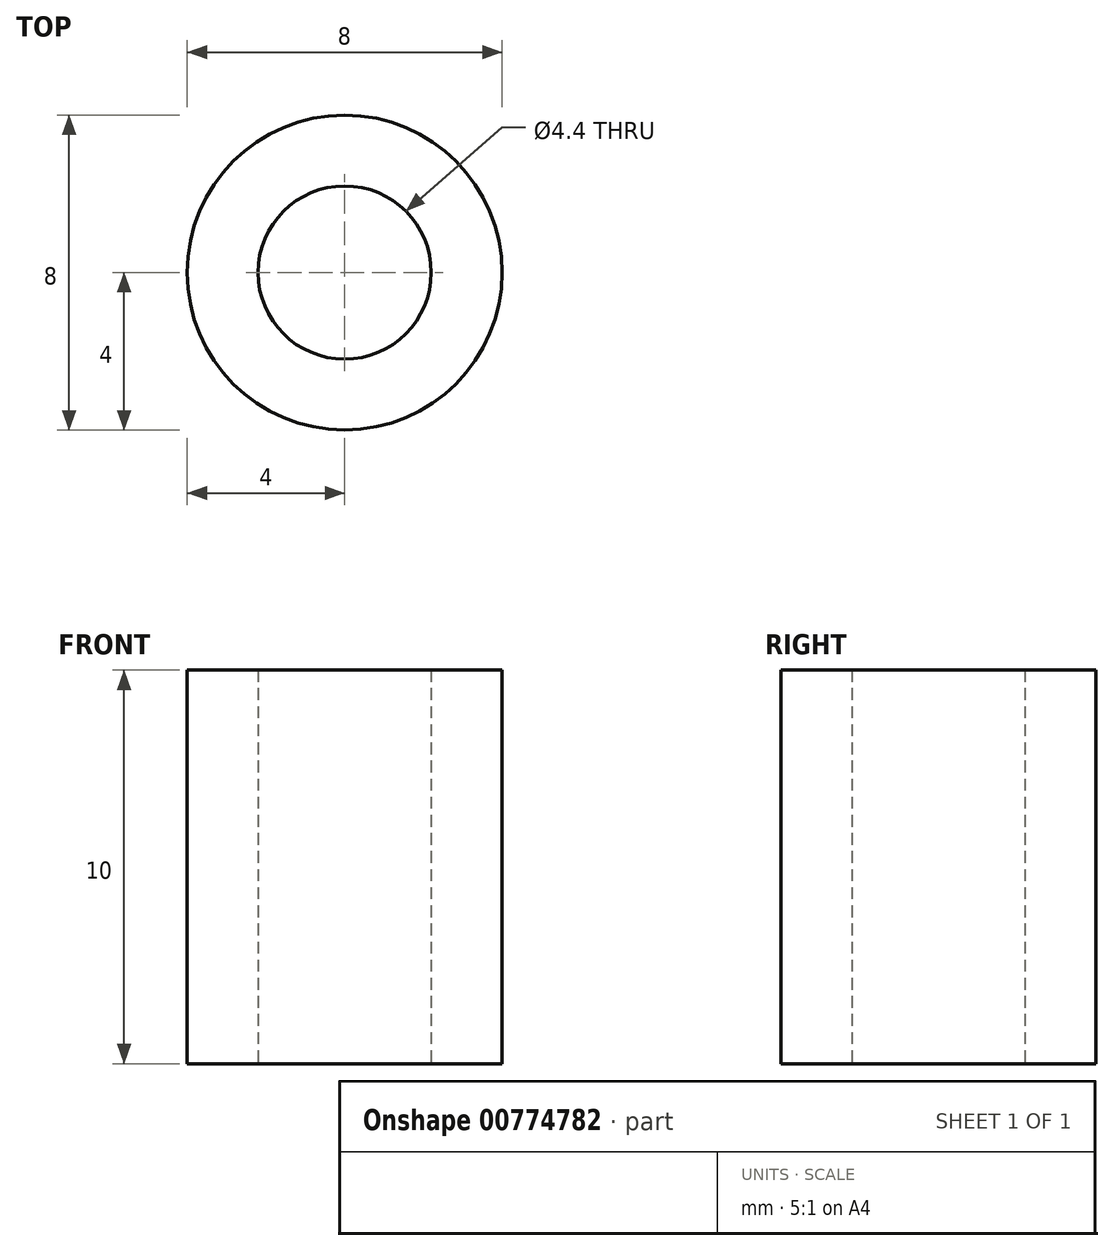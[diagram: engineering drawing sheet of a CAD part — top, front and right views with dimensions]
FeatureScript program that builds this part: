
annotation { "Feature Type Name" : "Feature", "Feature Type Description" : "" }
export const myFeature = defineFeature(function(context is Context, id is Id, definition is map)
    precondition{}
    {
        {
            var Q0;
            Q0=qCreatedBy(makeId("Top.planeOp"),FACE);
            var sketch = newSketch(context, id + "F0", { "sketchPlane" : qUnion([Q0])});
            skCircle(sketch, "E0", {"center": v(0, 0) * mm, "radius": 4 * mm});
            skSolve(sketch);
        }
        {
            var Q0;
            Q0 = qSketchRegion(id + "F0", true);
            extrude(context, id + "F1", {"entities" : qUnion([Q0]), "depth" : 10 * mm, "offsetDistance" : 25 * mm});
        }
        {
            var Q0;
            Q0=sQuery(id+"F0.wireOp",VERTEX,"E0.center");
            var Q1;
            Q1=makeQuery(id+"F1.opExtrude","SWEPT_BODY",BODY,{"disambiguationData":[OSD([sQuery(id+"F0.wireOp",EDGE,"E0")])]});
            hole(context, id + "F2", {"style" : HoleStyle.SIMPLE, "endStyle" : HoleEndStyle.THROUGH, "oppositeDirection" : true, "standardTappedOrClearance" : lookupTablePath({ "standard" : "ISO", "fit" : "Normal", "size" : "M4", "type" : "Clearance" }), "standardBlindInLast" : lookupTablePath({ "fit" : "Standard", "standard" : "ISO", "size" : "M4", "type" : "Clearance" }), "holeDiameter" : 4.4 * mm, "majorDiameter" : 5 * mm, "isTappedThrough" : true, "tappedDepth" : 12 * mm, "tapClearance" : 3, "locations" : qUnion([Q0]), "scope" : qUnion([Q1])});
        }
    });
